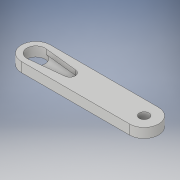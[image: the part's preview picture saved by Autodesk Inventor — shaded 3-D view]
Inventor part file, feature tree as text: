
AUTODESK INVENTOR PART (.ipt)
format: ipt  version: 2018.1 (Build 221171000, 171)  size: 124,928 bytes
history: native  units: mm
features: extrude x2, sketch x2
ambient origin geometry x8: Origin, YZ Plane, XZ Plane, XY Plane, X Axis, Y Axis, Z Axis, Center Point
bodies: Body1 (feature_tree)
feature tree (4):
  extrude  "Extrusion2"  Depth=12.0mm
  extrude  "Extrusion3"  Depth=45.0mm
  sketch  "Sketch1"  dims[d0=7.5mm d1=12.0mm]
  sketch  "Sketch2"  dims[d2=4.0mm d3=45.0mm d4=12.0mm d7=4.0mm d8=0.0mm d9=14.108mm d10=4.5mm d11=2.775mm d12=2.522276mm d13=5.55mm d18=2.0mm d19=0.0mm]
